# Revit family: Faucet-Single_Control-American_Standard-Colony_PRO-7074.100_Series
name_source: partatom
category: Plumbing Fixtures
units: mm (PartAtom-declared; Revit-internal decimal feet)

## family parameters
Always vertical = No
Cut with Voids When Loaded = No
OmniClass Number = 23.45.55.14
OmniClass Title = Single Faucets
Part Type = Normal
Room Calculation Point = No
Round Connector Dimension = Use Diameter
Shared = Yes
Work Plane-Based = Yes

## types (2) — shared parameters
ADA Compliant = Yes
Assembly Code = D2020300
CW Connection = No
CWFU = 1.5
Default Elevation = 0"
Description = Colony Pro Single Control Kitchen Faucet With Pull-Out Spray.
Flow Rate = 1.5 GPM (5.7L/min)
HW Connection = No
HWFU = 1.5
Height = 9 11/16"
Installation Type = Deck Mounted
Length = 10"
Manufacturer = American Standard
Price = Prices may vary. Please consult Manufacturer Representative for most up-to-date price list.
Product Documentation Link = https://americanstandard.box.com
Product Page URL = https://www.americanstandard-us.com
Revised Date = 09/14/2021
Tempered Water Connection = Yes
Tempered Water Connection Diameter = 3/8"
URL = http://www.americanstandard-us.com
Vent Connection = No
WFU = 2
Waste Connection = No
Width = 8 11/16"

## per-type parameters (varying)
| type | Finish | Material |
| 7074.100.002 | Metal-American Standard-002-Polished Chrome | Metal-American Standard-002-Polished Chrome |
| 7074.100.075 | Metal-American Standard-075-Stainless Steel | Metal-American Standard-075-Stainless Steel |

note: column(s) folded — value = type name in every type: Model

## geometry (parser evidence)
native form markers: Sweep x2
no freeform markers — native parametric forms only
